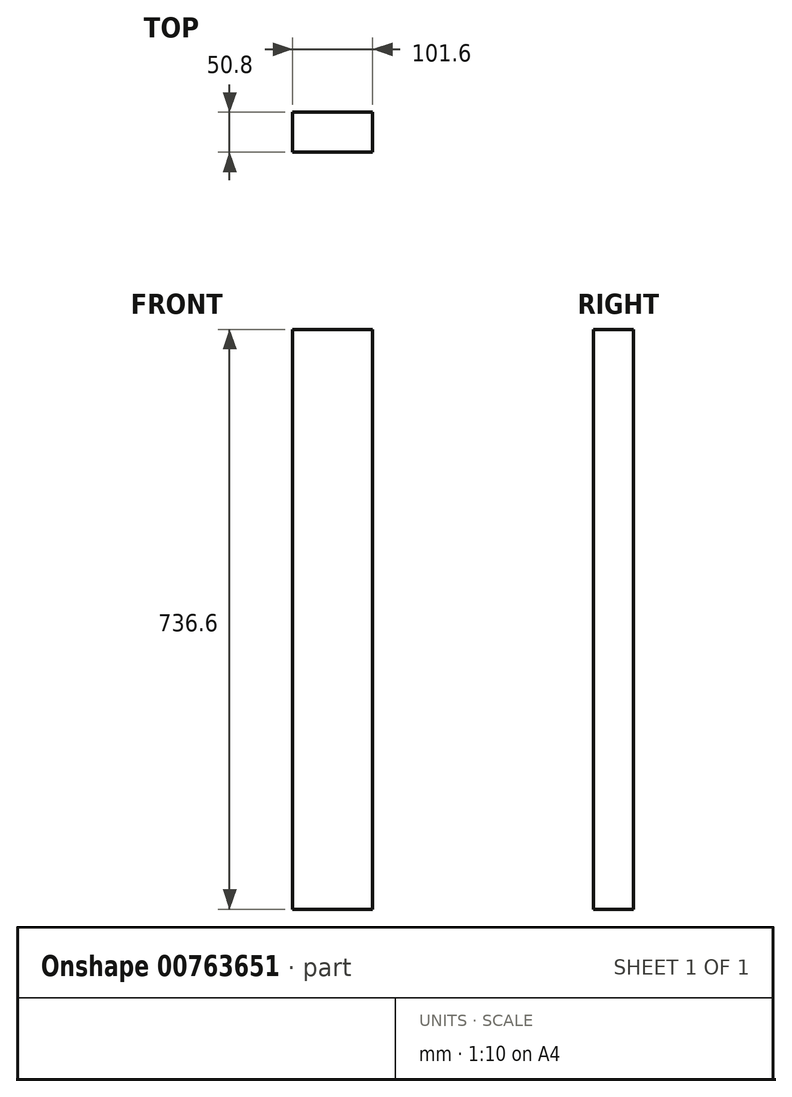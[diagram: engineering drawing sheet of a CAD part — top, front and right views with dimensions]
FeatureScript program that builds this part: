
annotation { "Feature Type Name" : "Feature", "Feature Type Description" : "" }
export const myFeature = defineFeature(function(context is Context, id is Id, definition is map)
    precondition{}
    {
        {
            var Q0;
            Q0=qCreatedBy(makeId("Front.planeOp"),FACE);
            var sketch = newSketch(context, id + "F0", { "sketchPlane" : qUnion([Q0])});
            skLineSegment(sketch, "E0.bottom", {"start": v(50.8, 368.3) * mm, "end": v(-50.8, 368.3) * mm});
            skLineSegment(sketch, "E0.top", {"start": v(50.8, -368.3) * mm, "end": v(-50.8, -368.3) * mm});
            skLineSegment(sketch, "E0.left", {"start": v(50.8, 368.3) * mm, "end": v(50.8, -368.3) * mm});
            skLineSegment(sketch, "E0.right", {"start": v(-50.8, 368.3) * mm, "end": v(-50.8, -368.3) * mm});
            skPoint(sketch, "E0.middle", {"position": v(0, 0) * mm});
            skSolve(sketch);
        }
        {
            var Q0;
            Q0 = qSketchRegion(id + "F0", true);
            extrude(context, id + "F1", {"entities" : qUnion([Q0]), "depth" : 50.8 * mm, "offsetDistance" : 25.4 * mm});
        }
    });
